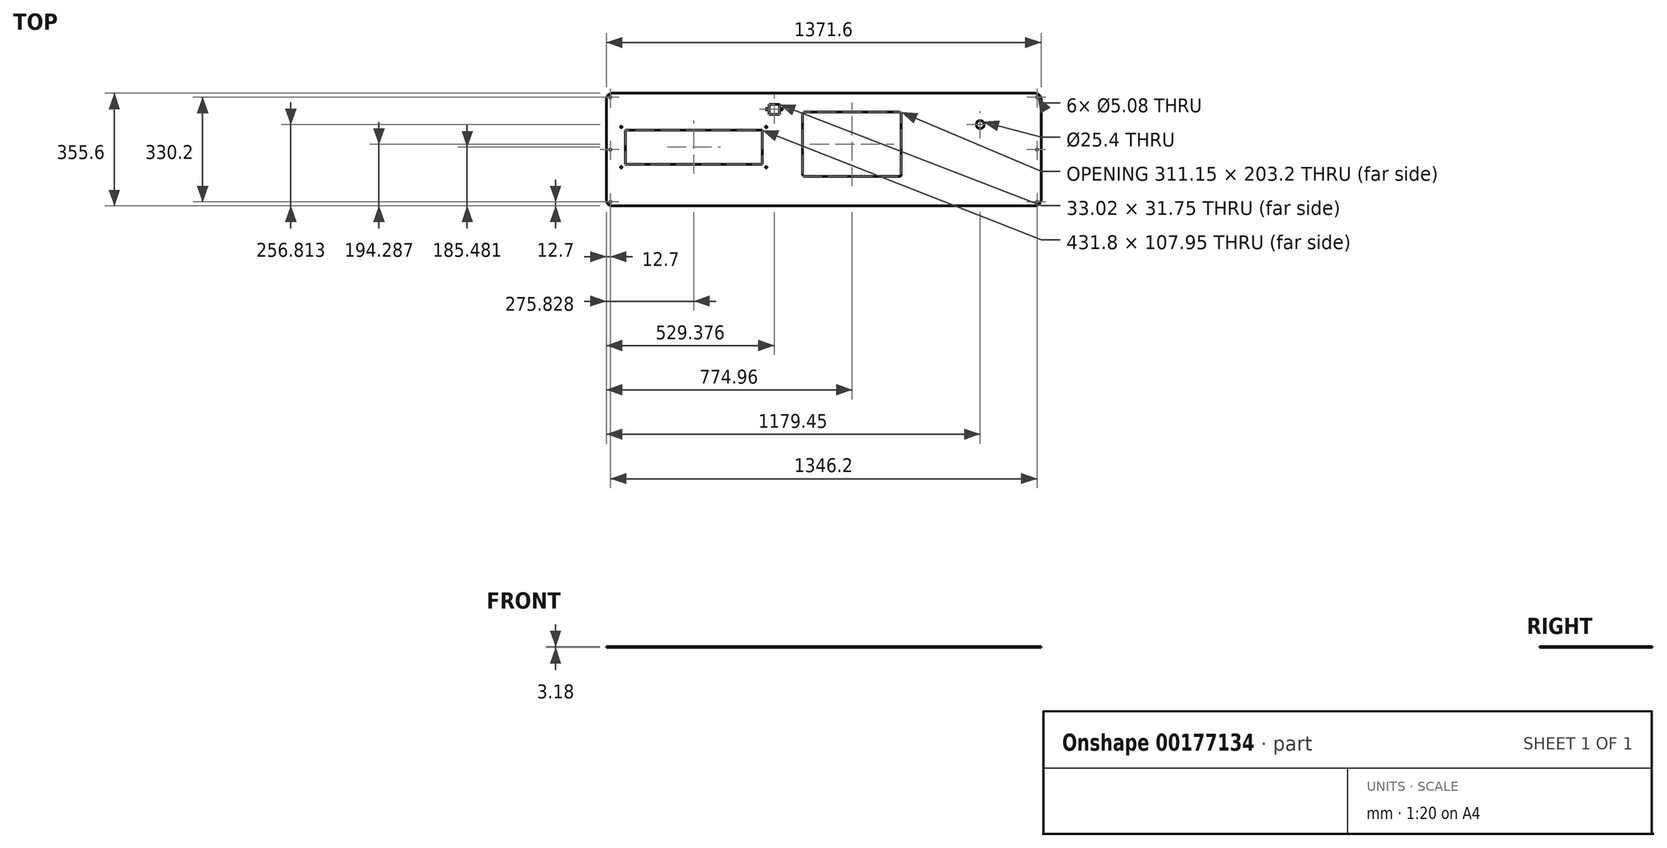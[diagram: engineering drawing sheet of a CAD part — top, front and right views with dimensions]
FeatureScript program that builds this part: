
annotation { "Feature Type Name" : "Feature", "Feature Type Description" : "" }
export const myFeature = defineFeature(function(context is Context, id is Id, definition is map)
    precondition{}
    {
        {
            var Q0;
            Q0=qCreatedBy(makeId("Top.planeOp"),FACE);
            var sketch = newSketch(context, id + "F0", { "sketchPlane" : qUnion([Q0])});
            skLineSegment(sketch, "E0.bottom", {"start": v(0, 0) * mm, "end": v(1371.6, 0) * mm});
            skLineSegment(sketch, "E0.top", {"start": v(0, 355.6) * mm, "end": v(1371.6, 355.6) * mm});
            skLineSegment(sketch, "E0.left", {"start": v(0, 0) * mm, "end": v(0, 355.6) * mm});
            skLineSegment(sketch, "E0.right", {"start": v(1371.6, 0) * mm, "end": v(1371.6, 355.6) * mm});
            skLineSegment(sketch, "E1.bottom", {"start": v(625.74, 295.89) * mm, "end": v(924.19, 295.89) * mm});
            skLineSegment(sketch, "E1.top", {"start": v(625.74, 92.69) * mm, "end": v(924.19, 92.69) * mm});
            skLineSegment(sketch, "E1.left", {"start": v(619.39, 289.54) * mm, "end": v(619.39, 99.04) * mm});
            skLineSegment(sketch, "E1.right", {"start": v(930.54, 289.54) * mm, "end": v(930.54, 99.04) * mm});
            skCircle(sketch, "E2", {"center": v(1179.46, 256.81) * mm, "radius": 12.7 * mm});
            skPoint(sketch, "E3.visualSharp", {"position": v(619.39, 295.89) * mm});
            skArc(sketch, "E3.filletArc", {"start": v(625.74, 295.89) * mm, "mid": v(621.24, 294.03) * mm, "end": v(619.39, 289.54) * mm});
            skPoint(sketch, "E4.visualSharp", {"position": v(619.39, 92.69) * mm});
            skArc(sketch, "E4.filletArc", {"start": v(619.39, 99.04) * mm, "mid": v(621.24, 94.55) * mm, "end": v(625.74, 92.69) * mm});
            skPoint(sketch, "E5.visualSharp", {"position": v(930.54, 92.69) * mm});
            skArc(sketch, "E5.filletArc", {"start": v(924.19, 92.69) * mm, "mid": v(928.68, 94.55) * mm, "end": v(930.54, 99.04) * mm});
            skPoint(sketch, "E6.visualSharp", {"position": v(930.54, 295.89) * mm});
            skArc(sketch, "E6.filletArc", {"start": v(930.54, 289.54) * mm, "mid": v(928.68, 294.03) * mm, "end": v(924.19, 295.89) * mm});
            skCircle(sketch, "E7", {"center": v(12.7, 342.9) * mm, "radius": 2.54 * mm});
            skCircle(sketch, "E8", {"center": v(12.7, 12.7) * mm, "radius": 2.54 * mm});
            skCircle(sketch, "E9", {"center": v(1358.9, 12.7) * mm, "radius": 2.54 * mm});
            skCircle(sketch, "E10", {"center": v(1358.9, 342.9) * mm, "radius": 2.54 * mm});
            skLineSegment(sketch, "E11.bottom", {"start": v(512.87, 320.99) * mm, "end": v(545.89, 320.99) * mm});
            skLineSegment(sketch, "E11.top", {"start": v(512.87, 289.24) * mm, "end": v(545.89, 289.24) * mm});
            skLineSegment(sketch, "E11.left", {"start": v(512.87, 320.99) * mm, "end": v(512.87, 289.24) * mm});
            skLineSegment(sketch, "E11.right", {"start": v(545.89, 320.99) * mm, "end": v(545.89, 289.24) * mm});
            skCircle(sketch, "E12", {"center": v(505.25, 305.11) * mm, "radius": 2.5 * mm});
            skCircle(sketch, "E13", {"center": v(553.5, 305.11) * mm, "radius": 2.5 * mm});
            skCircle(sketch, "E14", {"center": v(47.23, 248.98) * mm, "radius": 2.41 * mm});
            skCircle(sketch, "E15", {"center": v(504.43, 248.98) * mm, "radius": 2.41 * mm});
            skCircle(sketch, "E16", {"center": v(47.23, 121.98) * mm, "radius": 2.41 * mm});
            skCircle(sketch, "E17", {"center": v(504.43, 121.98) * mm, "radius": 2.41 * mm});
            skPoint(sketch, "E18", {"position": v(275.83, 185.48) * mm});
            skLineSegment(sketch, "E19.bottom", {"start": v(59.93, 239.46) * mm, "end": v(491.73, 239.46) * mm});
            skLineSegment(sketch, "E19.top", {"start": v(59.93, 131.5) * mm, "end": v(491.73, 131.5) * mm});
            skLineSegment(sketch, "E19.left", {"start": v(59.93, 239.46) * mm, "end": v(59.93, 131.5) * mm});
            skLineSegment(sketch, "E19.right", {"start": v(491.73, 239.46) * mm, "end": v(491.73, 131.5) * mm});
            skCircle(sketch, "E20", {"center": v(12.7, 177.8) * mm, "radius": 2.54 * mm});
            skCircle(sketch, "E21", {"center": v(1358.9, 177.8) * mm, "radius": 2.54 * mm});
            skSolve(sketch);
        }
        {
            var Q0;
            Q0=makeQuery(id+"F0.imprint","IMPRINT",FACE,{"disambiguationData":[TD([[makeQuery(id+"F0.imprint","IMPRINT",EDGE,{"derivedFrom":sQuery(id+"F0.wireOp",EDGE,"E0.bottom")}),1.0]])]});
            extrude(context, id + "F1", {"entities" : qUnion([Q0]), "depth" : 3.17 * mm});
        }
        {
            var Q0;
            Q0=makeQuery(id+"F1.opExtrude","SWEPT_EDGE",EDGE,{"disambiguationData":[OSD([sQuery(id+"F0.wireOp",EDGE,"E0.top"),sQuery(id+"F0.wireOp",EDGE,"E0.left")])]});
            var Q1;
            Q1=makeQuery(id+"F1.opExtrude","SWEPT_EDGE",EDGE,{"disambiguationData":[OSD([sQuery(id+"F0.wireOp",EDGE,"E0.bottom"),sQuery(id+"F0.wireOp",EDGE,"E0.left")])]});
            var Q2;
            Q2=makeQuery(id+"F1.opExtrude","SWEPT_EDGE",EDGE,{"disambiguationData":[OSD([sQuery(id+"F0.wireOp",EDGE,"E0.bottom"),sQuery(id+"F0.wireOp",EDGE,"E0.right")])]});
            var Q3;
            Q3=makeQuery(id+"F1.opExtrude","SWEPT_EDGE",EDGE,{"disambiguationData":[OSD([sQuery(id+"F0.wireOp",EDGE,"E0.top"),sQuery(id+"F0.wireOp",EDGE,"E0.right")])]});
            fillet(context, id + "F2", {"entities" : qUnion([Q0, Q1, Q2, Q3]), "radius" : 20.32 * mm, "tangentPropagation" : true, "allowEdgeOverflow" : false});
        }
    });
